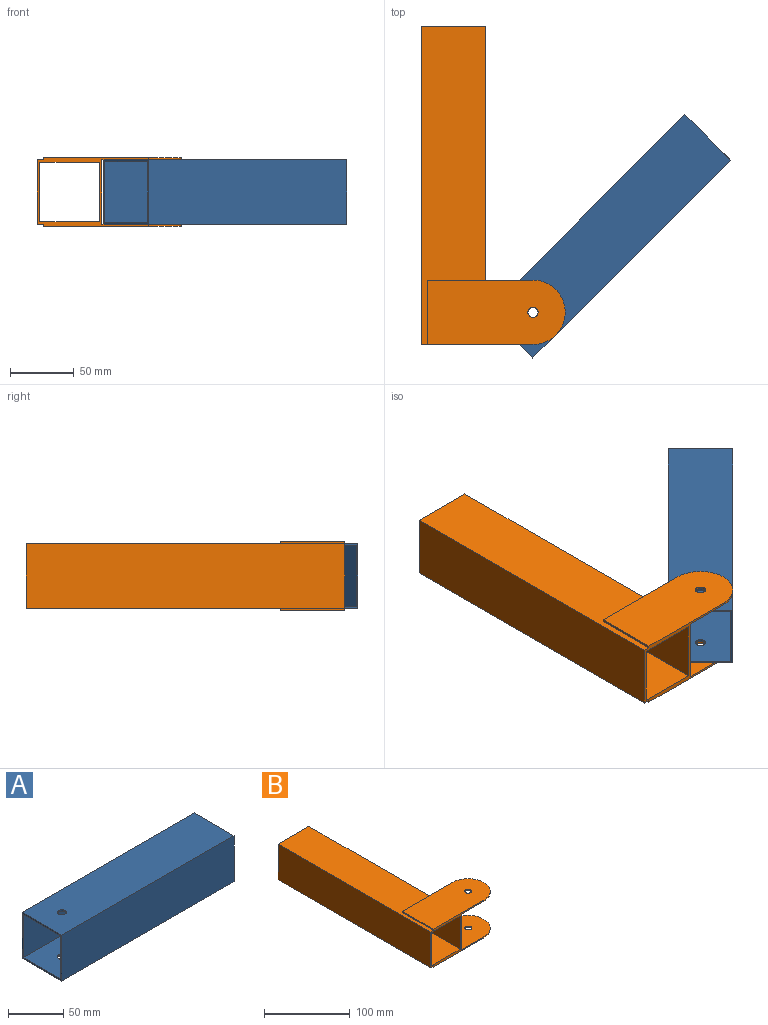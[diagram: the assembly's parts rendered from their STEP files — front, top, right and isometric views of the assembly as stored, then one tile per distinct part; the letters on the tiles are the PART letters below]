
ASSEMBLY  parts=2 mates=1
PART A: 12 faces, bbox 220x50.8x50.8 mm
  f0: plane 220x47.6mm, normal (0,1,0), area 10472mm2, adj f1,f7,f8,f9
  f1: plane 220x47.6mm, normal (0,0,-1), area 10421.7mm2, adj f0,f2,f8,f9,f11
  f2: plane 220x47.6mm, normal (0,-1,0), area 10472mm2, adj f1,f7,f8,f9
  f3: plane 220x50.8mm, normal (0,1,0), area 11176mm2, adj f4,f6,f8,f9
  f4: plane 220x50.8mm, normal (0,0,1), area 11125.7mm2, adj f3,f5,f8,f9,f11
  f5: plane 220x50.8mm, normal (0,-1,0), area 11176mm2, adj f4,f6,f8,f9
  f6: plane 220x50.8mm, normal (0,0,-1), area 11125.7mm2, adj f3,f5,f8,f9,f10
  f7: plane 220x47.6mm, normal (0,0,1), area 10421.7mm2, adj f0,f2,f8,f9,f10
  f8: plane 50.8x50.8mm, normal (1,0,0), area 314.9mm2, adj f0,f1,f2,f3,f4,f5,f6,f7
  f9: plane 50.8x50.8mm, normal (-1,0,0), area 314.9mm2, adj f0,f1,f2,f3,f4,f5,f6,f7
  f10: cylinder r=4mm len=8mm, axis (0,0,1), area 40.2mm2, adj f6,f7
  f11: cylinder r=4mm len=8mm, axis (0,0,1), area 40.2mm2, adj f1,f4
PART B: 22 faces, bbox 113.2x250.8x54 mm
  f0: plane 250.8x47.2mm, normal (1,0,0), area 11837.8mm2, adj f1,f7,f8,f9
  f1: plane 250.8x47.2mm, normal (0,0,-1), area 11837.8mm2, adj f0,f2,f8,f9
  f2: plane 250.8x47.2mm, normal (-1,0,0), area 11837.8mm2, adj f1,f7,f8,f9
  f3: plane 250.8x50.8mm, normal (1,0,0), area 12740.6mm2, adj f4,f6,f8,f9,f10,f16
  f4: plane 250.8x50.8mm, normal (0,0,1), area 10414mm2, adj f3,f5,f8,f9,f11,f12
  f5: plane 250.8x50.8mm, normal (-1,0,0), area 12740.6mm2, adj f4,f6,f8,f9
  f6: plane 250.8x50.8mm, normal (0,0,-1), area 10414mm2, adj f3,f5,f8,f9,f17,f18
  f7: plane 250.8x47.2mm, normal (0,0,1), area 11837.8mm2, adj f0,f2,f8,f9
  f8: plane 87.8x54mm, normal (0,-1,0), area 617.8mm2, adj f0,f1,f2,f3,f4,f5,f6,f7
  f9: plane 50.8x50.8mm, normal (0,1,0), area 352.8mm2, adj f0,f1,f2,f3,f4,f5,f6,f7
  f10: plane 62.4x50.8mm, normal (0,0,-1), area 2842.7mm2, adj f3,f8,f11,f13,f14
  f11: plane 82.8x1.6mm, normal (0,1,0), area 132.5mm2, adj f4,f10,f12,f13,f15
  f12: plane 50.8x1.6mm, normal (-1,0,0), area 81.3mm2, adj f4,f8,f11,f15
  f13: cylinder r=25.4mm len=50.8mm, axis (0,0,-1), area 127.7mm2, adj f8,f10,f11,f15
  f14: cylinder r=4mm len=8mm, axis (0,0,-1), area 40.2mm2, adj f10,f15
  f15: plane 108.2x50.8mm, normal (0,0,1), area 5169.4mm2, adj f8,f11,f12,f13,f14
  f16: plane 62.4x50.8mm, normal (0,0,1), area 2842.7mm2, adj f3,f8,f17,f19,f20
  f17: plane 82.8x1.6mm, normal (0,1,0), area 132.5mm2, adj f6,f16,f18,f19,f21
  f18: plane 50.8x1.6mm, normal (-1,0,0), area 81.3mm2, adj f6,f8,f17,f21
  f19: cylinder r=25.4mm len=50.8mm, axis (0,0,1), area 127.7mm2, adj f8,f16,f17,f21
  f20: cylinder r=4mm len=8mm, axis (0,0,1), area 40.2mm2, adj f16,f21
  f21: plane 108.2x50.8mm, normal (0,0,-1), area 5169.4mm2, adj f8,f17,f18,f19,f20
PLACE A rot(axis=(0,0,1),45deg) t=(-45.31,-39.81,0)mm
PLACE B at identity
MATE revolute A.f10 <-> B.f19  axis (0,0,1) through (25.4,-74.6,25.4)mm
